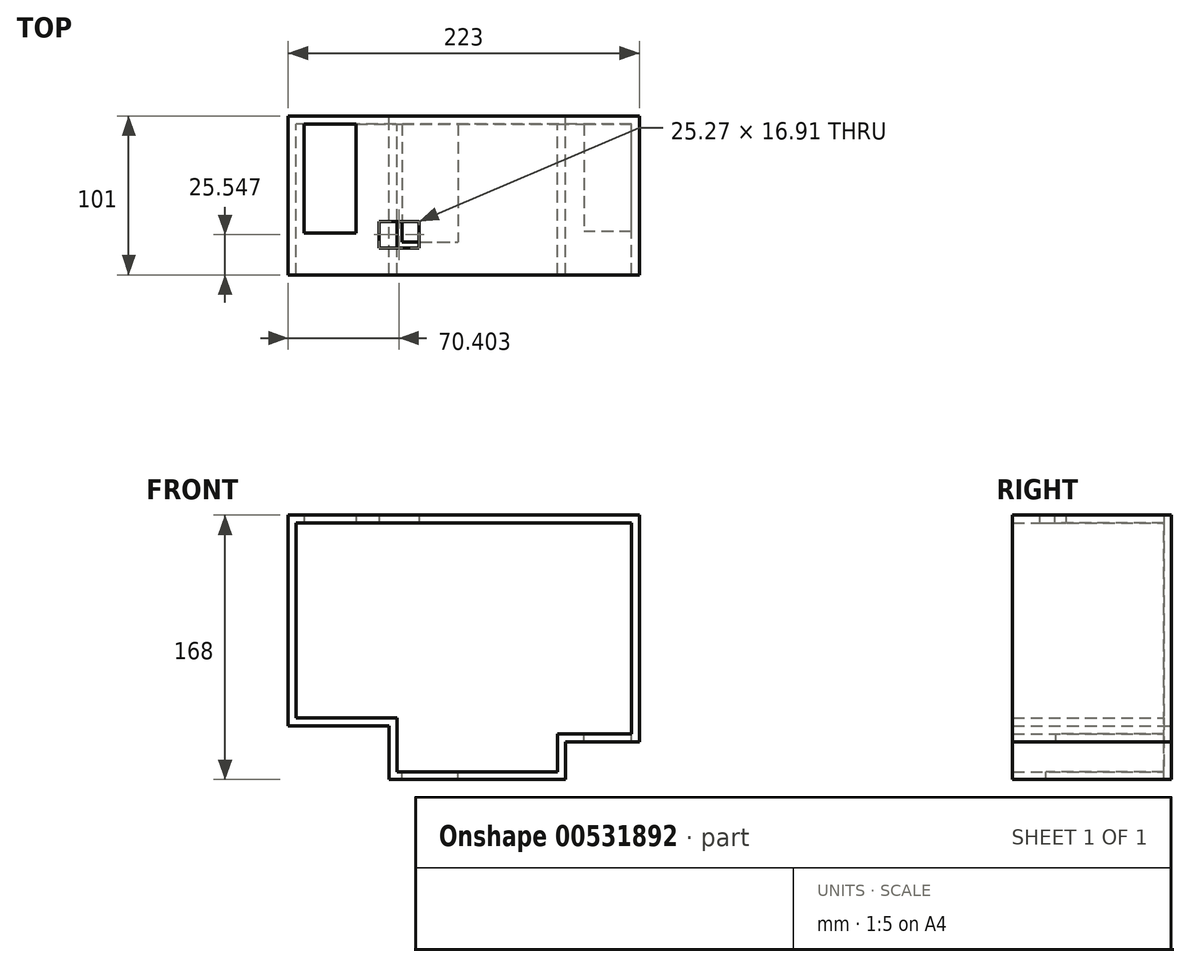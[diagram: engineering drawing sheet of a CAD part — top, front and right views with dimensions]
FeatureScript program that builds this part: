
annotation { "Feature Type Name" : "Feature", "Feature Type Description" : "" }
export const myFeature = defineFeature(function(context is Context, id is Id, definition is map)
    precondition{}
    {
        {
            var Q0;
            Q0=qCreatedBy(makeId("Front.planeOp"),FACE);
            var sketch = newSketch(context, id + "F0", { "sketchPlane" : qUnion([Q0])});
            skLineSegment(sketch, "E0", {"start": v(0, 0) * mm, "end": v(102, 0) * mm});
            skLineSegment(sketch, "E1", {"start": v(102, 0) * mm, "end": v(102, 24) * mm});
            skLineSegment(sketch, "E2", {"start": v(102, 24) * mm, "end": v(149, 24) * mm});
            skLineSegment(sketch, "E3", {"start": v(149, 24) * mm, "end": v(149, 158) * mm});
            skLineSegment(sketch, "E4", {"start": v(149, 158) * mm, "end": v(-64, 158) * mm});
            skLineSegment(sketch, "E5", {"start": v(-64, 158) * mm, "end": v(-64, 34) * mm});
            skLineSegment(sketch, "E6", {"start": v(-64, 34) * mm, "end": v(0, 34) * mm});
            skLineSegment(sketch, "E7", {"start": v(0, 34) * mm, "end": v(0, 0) * mm});
            skLineSegment(sketch, "E8", {"start": v(0, -5) * mm, "end": v(102, -5) * mm});
            skLineSegment(sketch, "E9", {"start": v(102, -5) * mm, "end": v(107, -5) * mm});
            skLineSegment(sketch, "E10", {"start": v(107, -5) * mm, "end": v(107, 19) * mm});
            skLineSegment(sketch, "E11", {"start": v(107, 19) * mm, "end": v(154, 19) * mm});
            skLineSegment(sketch, "E12", {"start": v(154, 19) * mm, "end": v(154, 163) * mm});
            skLineSegment(sketch, "E13", {"start": v(154, 163) * mm, "end": v(-69, 163) * mm});
            skLineSegment(sketch, "E14", {"start": v(-69, 163) * mm, "end": v(-69, 29) * mm});
            skLineSegment(sketch, "E15", {"start": v(-69, 29) * mm, "end": v(-5, 29) * mm});
            skLineSegment(sketch, "E16", {"start": v(-5, 29) * mm, "end": v(-5, -5) * mm});
            skLineSegment(sketch, "E17", {"start": v(-5, -5) * mm, "end": v(0, -5) * mm});
            skSolve(sketch);
        }
        {
            var Q0;
            Q0 = qSketchRegion(id + "F0", true);
            extrude(context, id + "F1", {"entities" : qUnion([Q0]), "depth" : 96 * mm, "offsetDistance" : 25 * mm});
        }
        {
            var Q0;
            Q0=makeQuery(id+"F1.opExtrude","CAP_FACE",FACE,{"disambiguationData":[OSD([sQuery(id+"F0.wireOp",EDGE,"E0"),sQuery(id+"F0.wireOp",EDGE,"E1"),sQuery(id+"F0.wireOp",EDGE,"E2"),sQuery(id+"F0.wireOp",EDGE,"E3"),sQuery(id+"F0.wireOp",EDGE,"E4"),sQuery(id+"F0.wireOp",EDGE,"E5"),sQuery(id+"F0.wireOp",EDGE,"E6"),sQuery(id+"F0.wireOp",EDGE,"E7"),sQuery(id+"F0.wireOp",EDGE,"E8"),sQuery(id+"F0.wireOp",EDGE,"E9"),sQuery(id+"F0.wireOp",EDGE,"E10"),sQuery(id+"F0.wireOp",EDGE,"E11"),sQuery(id+"F0.wireOp",EDGE,"E12"),sQuery(id+"F0.wireOp",EDGE,"E13"),sQuery(id+"F0.wireOp",EDGE,"E14"),sQuery(id+"F0.wireOp",EDGE,"E15"),sQuery(id+"F0.wireOp",EDGE,"E16"),sQuery(id+"F0.wireOp",EDGE,"E17")])],"isStart":true});
            var sketch = newSketch(context, id + "F2", { "sketchPlane" : qUnion([Q0])});
            skLineSegment(sketch, "E18", {"start": v(-154, 163) * mm, "end": v(69, 163) * mm});
            skLineSegment(sketch, "E19", {"start": v(69, 163) * mm, "end": v(69, 29) * mm});
            skLineSegment(sketch, "E20", {"start": v(69, 29) * mm, "end": v(5, 29) * mm});
            skLineSegment(sketch, "E21", {"start": v(5, 29) * mm, "end": v(5, -5) * mm});
            skLineSegment(sketch, "E22", {"start": v(5, -5) * mm, "end": v(-107, -5) * mm});
            skLineSegment(sketch, "E23", {"start": v(-107, -5) * mm, "end": v(-107, 19) * mm});
            skLineSegment(sketch, "E24", {"start": v(-107, 19) * mm, "end": v(-154, 19) * mm});
            skLineSegment(sketch, "E25", {"start": v(-154, 19) * mm, "end": v(-154, 163) * mm});
            skSolve(sketch);
        }
        {
            var Q0;
            Q0 = qSketchRegion(id + "F2", true);
            extrude(context, id + "F3", {"entities" : qUnion([Q0]), "operationType" : NewBodyOperationType.ADD, "depth" : 5 * mm, "offsetDistance" : 25 * mm});
        }
        {
            var Q0;
            Q0=makeQuery(id+"F1.opExtrude","SWEPT_FACE",FACE,{"disambiguationData":[OSD([sQuery(id+"F0.wireOp",EDGE,"E0")])]});
            var sketch = newSketch(context, id + "F4", { "sketchPlane" : qUnion([Q0])});
            skLineSegment(sketch, "E26.bottom", {"start": v(3.32, 0) * mm, "end": v(39, 0) * mm});
            skLineSegment(sketch, "E26.top", {"start": v(3.32, -74.97) * mm, "end": v(39, -74.97) * mm});
            skLineSegment(sketch, "E26.left", {"start": v(3.32, 0) * mm, "end": v(3.32, -74.97) * mm});
            skLineSegment(sketch, "E26.right", {"start": v(39, 0) * mm, "end": v(39, -74.97) * mm});
            skSolve(sketch);
        }
        {
            var Q0;
            Q0 = qSketchRegion(id + "F4", true);
            extrude(context, id + "F5", {"entities" : qUnion([Q0]), "operationType" : NewBodyOperationType.REMOVE, "oppositeDirection" : true, "depth" : 25 * mm, "offsetDistance" : 25 * mm});
        }
        {
            var Q0;
            Q0=makeQuery(id+"F1.opExtrude","SWEPT_FACE",FACE,{"disambiguationData":[OSD([sQuery(id+"F0.wireOp",EDGE,"E2")])]});
            var sketch = newSketch(context, id + "F6", { "sketchPlane" : qUnion([Q0])});
            skLineSegment(sketch, "E27.bottom", {"start": v(149, 0) * mm, "end": v(119, 0) * mm});
            skLineSegment(sketch, "E27.top", {"start": v(149, -68.4) * mm, "end": v(119, -68.4) * mm});
            skLineSegment(sketch, "E27.left", {"start": v(149, 0) * mm, "end": v(149, -68.4) * mm});
            skLineSegment(sketch, "E27.right", {"start": v(119, 0) * mm, "end": v(119, -68.4) * mm});
            skSolve(sketch);
        }
        {
            var Q0;
            Q0 = qSketchRegion(id + "F6", true);
            extrude(context, id + "F7", {"entities" : qUnion([Q0]), "operationType" : NewBodyOperationType.REMOVE, "oppositeDirection" : true, "depth" : 25 * mm, "offsetDistance" : 25 * mm});
        }
        {
            var Q0;
            Q0=makeQuery(id+"F1.opExtrude","SWEPT_FACE",FACE,{"disambiguationData":[OSD([sQuery(id+"F0.wireOp",EDGE,"E4")])]});
            var sketch = newSketch(context, id + "F8", { "sketchPlane" : qUnion([Q0])});
            skLineSegment(sketch, "E28.bottom", {"start": v(-58.9, 0) * mm, "end": v(-26, 0) * mm});
            skLineSegment(sketch, "E28.top", {"start": v(-58.9, 69.47) * mm, "end": v(-26, 69.47) * mm});
            skLineSegment(sketch, "E28.left", {"start": v(-58.9, 0) * mm, "end": v(-58.9, 69.47) * mm});
            skLineSegment(sketch, "E28.right", {"start": v(-26, 0) * mm, "end": v(-26, 69.47) * mm});
            skSolve(sketch);
        }
        {
            var Q0;
            Q0 = qSketchRegion(id + "F8", true);
            extrude(context, id + "F9", {"entities" : qUnion([Q0]), "operationType" : NewBodyOperationType.REMOVE, "oppositeDirection" : true, "depth" : 25 * mm, "offsetDistance" : 25 * mm});
        }
        {
            var Q0;
            Q0=makeQuery(id+"F1.opExtrude","SWEPT_FACE",FACE,{"disambiguationData":[OSD([sQuery(id+"F0.wireOp",EDGE,"E4")])]});
            var sketch = newSketch(context, id + "F10", { "sketchPlane" : qUnion([Q0])});
            skLineSegment(sketch, "E29.bottom", {"start": v(-11.23, 78.9) * mm, "end": v(14.04, 78.9) * mm});
            skLineSegment(sketch, "E29.top", {"start": v(-11.23, 62) * mm, "end": v(14.04, 62) * mm});
            skLineSegment(sketch, "E29.left", {"start": v(-11.23, 78.9) * mm, "end": v(-11.23, 62) * mm});
            skLineSegment(sketch, "E29.right", {"start": v(14.04, 78.9) * mm, "end": v(14.04, 62) * mm});
            skSolve(sketch);
        }
        {
            var Q0;
            Q0 = qSketchRegion(id + "F10", true);
            extrude(context, id + "F11", {"entities" : qUnion([Q0]), "operationType" : NewBodyOperationType.REMOVE, "oppositeDirection" : true, "depth" : 25 * mm, "offsetDistance" : 25 * mm});
        }
    });
